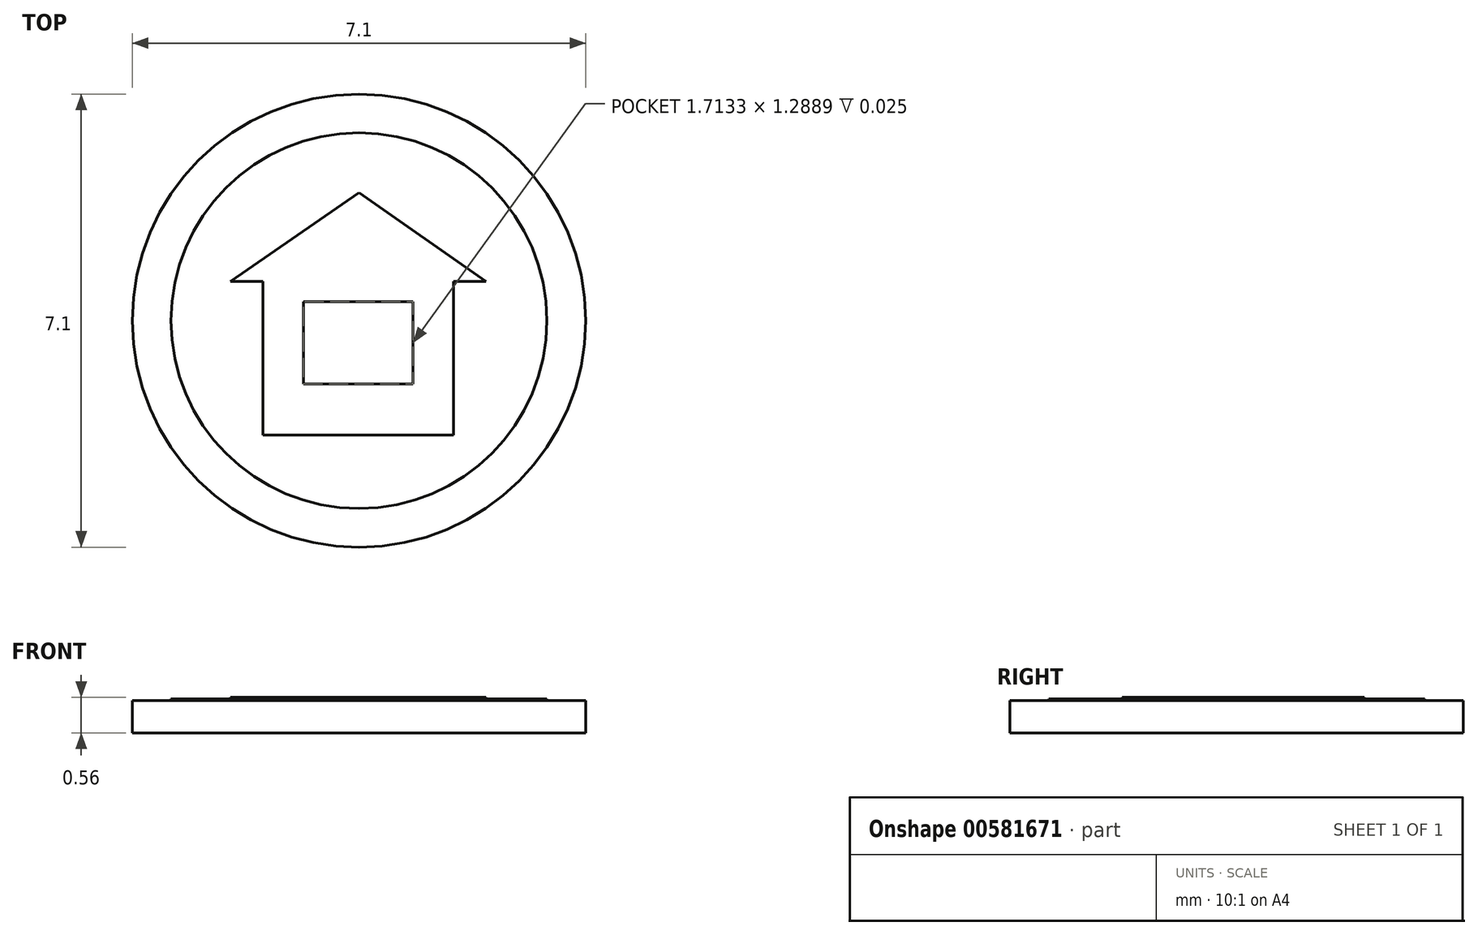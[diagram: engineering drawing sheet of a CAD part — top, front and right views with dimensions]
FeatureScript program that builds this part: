
annotation { "Feature Type Name" : "Feature", "Feature Type Description" : "" }
export const myFeature = defineFeature(function(context is Context, id is Id, definition is map)
    precondition{}
    {
        {
            var Q0;
            Q0=qCreatedBy(makeId("Top.planeOp"),FACE);
            var sketch = newSketch(context, id + "F0", { "sketchPlane" : qUnion([Q0])});
            skCircle(sketch, "E0", {"center": v(0, 0) * mm, "radius": 3.55 * mm});
            skSolve(sketch);
        }
        {
            var Q0;
            Q0 = qSketchRegion(id + "F0", true);
            extrude(context, id + "F1", {"entities" : qUnion([Q0]), "depth" : 0.5 * mm, "offsetDistance" : 25.4 * mm});
        }
        {
            var Q0;
            Q0=makeQuery(id+"F1.opExtrude","CAP_FACE",FACE,{"disambiguationData":[OSD([sQuery(id+"F0.wireOp",EDGE,"E0")])],"isStart":false});
            var sketch = newSketch(context, id + "F2", { "sketchPlane" : qUnion([Q0])});
            skCircle(sketch, "E1", {"center": v(0, 0) * mm, "radius": 2.94 * mm});
            skSolve(sketch);
        }
        {
            var Q0;
            Q0 = qSketchRegion(id + "F2", true);
            extrude(context, id + "F3", {"entities" : qUnion([Q0]), "operationType" : NewBodyOperationType.ADD, "depth" : 0.03 * mm, "offsetDistance" : 25.4 * mm});
        }
        {
            var Q0;
            Q0=makeQuery(id+"F3.opExtrude","CAP_FACE",FACE,{"disambiguationData":[OSD([sQuery(id+"F2.wireOp",EDGE,"E1")])],"isStart":false});
            var sketch = newSketch(context, id + "F4", { "sketchPlane" : qUnion([Q0])});
            skLineSegment(sketch, "E2", {"start": v(1.48, -1.8) * mm, "end": v(-1.5, -1.8) * mm});
            skLineSegment(sketch, "E3", {"start": v(-1.5, -1.8) * mm, "end": v(-1.5, 0.61) * mm});
            skLineSegment(sketch, "E4", {"start": v(-1.5, 0.61) * mm, "end": v(-2.01, 0.61) * mm});
            skLineSegment(sketch, "E5", {"start": v(-2.01, 0.61) * mm, "end": v(0, 2) * mm});
            skLineSegment(sketch, "E6", {"start": v(0, 2) * mm, "end": v(1.99, 0.61) * mm});
            skLineSegment(sketch, "E7", {"start": v(1.99, 0.61) * mm, "end": v(1.48, 0.61) * mm});
            skLineSegment(sketch, "E8", {"start": v(1.48, 0.61) * mm, "end": v(1.48, -1.8) * mm});
            skLineSegment(sketch, "E9", {"start": v(0.85, 0.3) * mm, "end": v(0.85, -1) * mm});
            skLineSegment(sketch, "E10", {"start": v(0.85, -1) * mm, "end": v(-0.87, -1) * mm});
            skLineSegment(sketch, "E11", {"start": v(-0.87, -1) * mm, "end": v(-0.87, 0.3) * mm});
            skLineSegment(sketch, "E12", {"start": v(-0.87, 0.3) * mm, "end": v(0.85, 0.3) * mm});
            skSolve(sketch);
        }
        {
            var Q0;
            Q0 = qSketchRegion(id + "F4", true);
            extrude(context, id + "F5", {"entities" : qUnion([Q0]), "operationType" : NewBodyOperationType.ADD, "depth" : 0.03 * mm, "offsetDistance" : 25.4 * mm});
        }
    });
